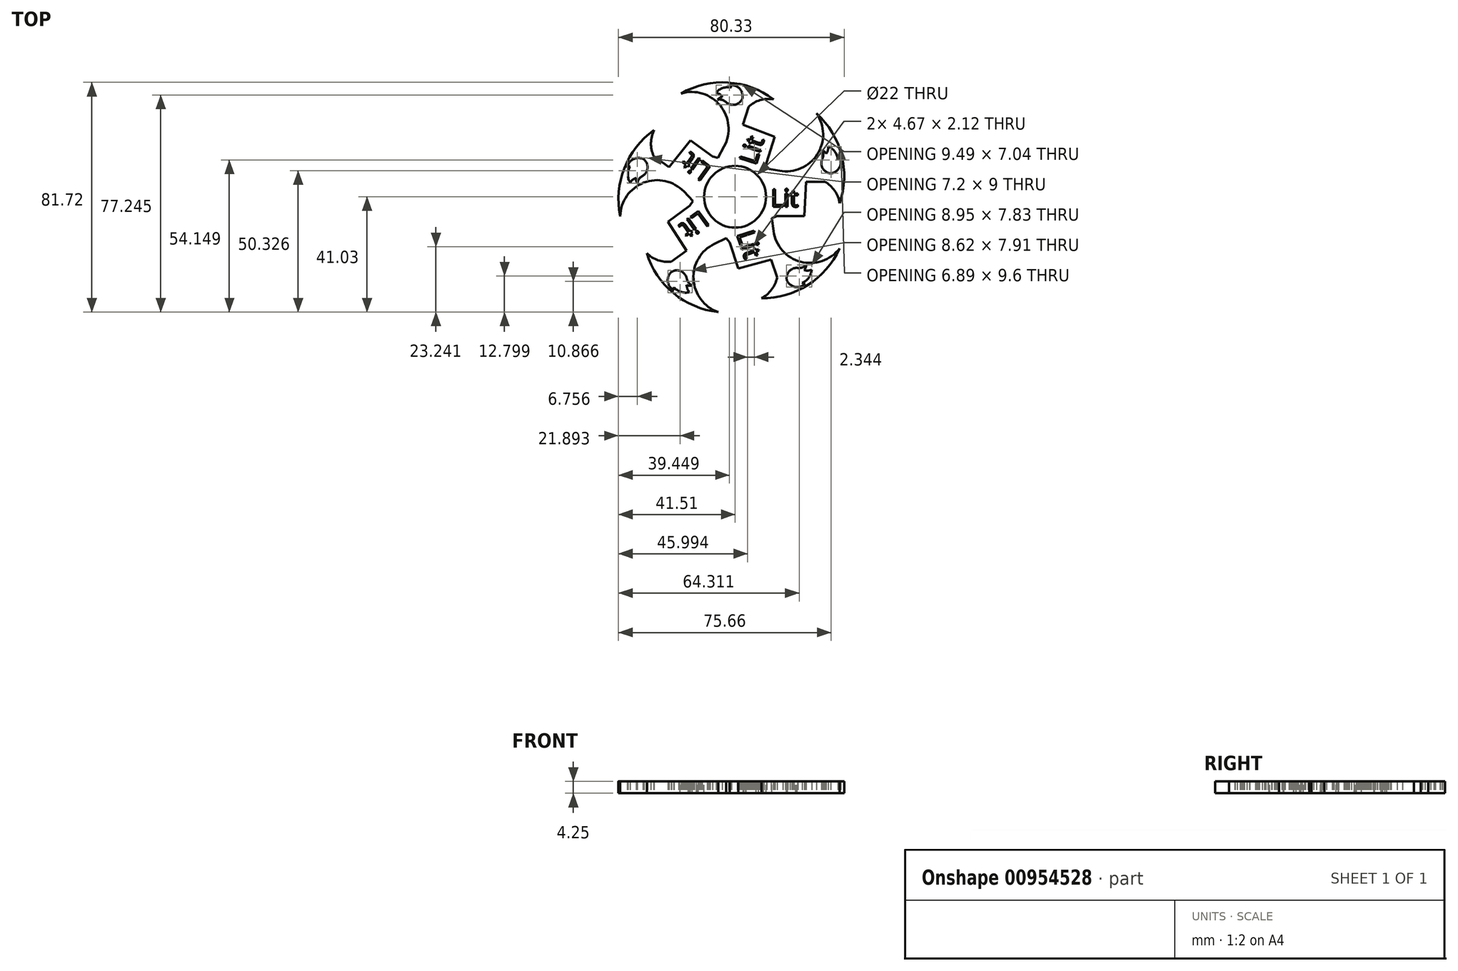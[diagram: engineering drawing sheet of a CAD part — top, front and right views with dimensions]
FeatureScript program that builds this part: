
annotation { "Feature Type Name" : "Feature", "Feature Type Description" : "" }
export const myFeature = defineFeature(function(context is Context, id is Id, definition is map)
    precondition{}
    {
        {
            var Q0;
            Q0=qCreatedBy(makeId("Top.planeOp"),FACE);
            var sketch = newSketch(context, id + "F0", { "sketchPlane" : qUnion([Q0])});
            skCircle(sketch, "E0", {"center": v(0, 0) * mm, "radius": 11 * mm});
            skArc(sketch, "E1", {"start": v(5, 13.33) * mm, "mid": v(-14.23, -0.3) * mm, "end": v(5.54, -13.11) * mm});
            skLineSegment(sketch, "E2", {"start": v(5, 13.33) * mm, "end": v(18.62, 10.86) * mm});
            skLineSegment(sketch, "E3", {"start": v(17.57, -8.04) * mm, "end": v(5.54, -13.11) * mm});
            skArc(sketch, "E4", {"start": v(18.62, 10.86) * mm, "mid": v(34.38, 17.7) * mm, "end": v(34.12, 34.88) * mm});
            skArc(sketch, "E5", {"start": v(43.79, -2.66) * mm, "mid": v(44.56, 17.56) * mm, "end": v(34.12, 34.88) * mm});
            skArc(sketch, "E6", {"start": v(43.79, -2.66) * mm, "mid": v(41.71, 2.53) * mm, "end": v(37.56, 6.26) * mm});
            skLineSegment(sketch, "E7", {"start": v(28.99, -8.04) * mm, "end": v(17.57, -8.04) * mm});
            skText(sketch, "E8", { "text": "Lit", "fontName": "OpenSans-Regular.ttf"});
            skLineSegment(sketch, "E9", {"start": v(28.99, -8.04) * mm, "end": v(29.68, 6.26) * mm});
            skLineSegment(sketch, "E10", {"start": v(29.68, 6.26) * mm, "end": v(37.56, 6.26) * mm});
            skPoint(sketch, "E11.orphan", {"position": v(0, -15.45) * mm});
            skPoint(sketch, "E12.orphan", {"position": v(0, 14.24) * mm});
            skPoint(sketch, "E13", {"position": v(14.9, -0.51) * mm});
            skLineSegment(sketch, "E14", {"start": v(0, 0) * mm, "end": v(28.23, 0) * mm, "construction": true});
            skArc(sketch, "E15", {"start": v(53.93, 19) * mm, "mid": v(54.3, 14.66) * mm, "end": v(58.04, 12.4) * mm});
            skArc(sketch, "E16", {"start": v(53.93, 19) * mm, "mid": v(54.47, 21.2) * mm, "end": v(53.93, 23.4) * mm});
            skArc(sketch, "E17", {"start": v(55.9, 21.72) * mm, "mid": v(55.05, 22.72) * mm, "end": v(53.93, 23.4) * mm});
            skArc(sketch, "E18", {"start": v(55.9, 21.72) * mm, "mid": v(56.67, 23.38) * mm, "end": v(56.82, 25.2) * mm});
            skArc(sketch, "E19", {"start": v(61.39, 19) * mm, "mid": v(59.97, 22.75) * mm, "end": v(56.82, 25.2) * mm});
            skArc(sketch, "E20", {"start": v(61.39, 19) * mm, "mid": v(61.87, 19.5) * mm, "end": v(62.21, 20.1) * mm});
            skArc(sketch, "E21", {"start": v(58.04, 12.4) * mm, "mid": v(62.14, 15.17) * mm, "end": v(62.21, 20.1) * mm});
            skLineSegment(sketch, "E22", {"start": v(33.75, 10.42) * mm, "end": v(57.45, 17.7) * mm, "construction": true});
            const initialGuessF0  = {"E8": [0.0149, -0.0042, 1, 0, 0.0074]};
            skSetInitialGuess(sketch, initialGuessF0);
            skSolve(sketch);
        }
        {
            var Q0;
            {var subQ0=sQuery(id+"F0.wireOp",EDGE,"JTTCuKp4-XvGG-GW8C-2jKd-2rtZk9alwzh2");var subQ1=sQuery(id+"F0.wireOp",EDGE,"M8TAi26V-Dveo-5j7V-sgvR-S3i7NmxKgKMn");var subQ2=makeQuery(id+"F0.imprint","INTERSECT",VERTEX,{"derivedFrom":[subQ1,subQ0]});Q0=makeQuery(id+"F0.imprint","IMPRINT",FACE,{"disambiguationData":[TD([[makeQuery(id+"F0.imprint","IMPRINT",EDGE,{"disambiguationData":[TD([[subQ2,1.0]])],"derivedFrom":subQ1}),-1.0]])]});}
            var Q1;
            {var subQ0=sQuery(id+"F0.wireOp",EDGE,"JTTCuKp4-XvGG-GW8C-2jKd-2rtZk9alwzh2");var subQ1=sQuery(id+"F0.wireOp",EDGE,"M8TAi26V-Dveo-5j7V-sgvR-S3i7NmxKgKMn");var subQ2=makeQuery(id+"F0.imprint","INTERSECT",VERTEX,{"derivedFrom":[subQ1,subQ0]});Q1=makeQuery(id+"F0.imprint","IMPRINT",FACE,{"disambiguationData":[TD([[makeQuery(id+"F0.imprint","IMPRINT",EDGE,{"disambiguationData":[TD([[subQ2,1.0]])],"derivedFrom":subQ1}),1.0]])]});}
            var Q2;
            {var subQ0=sQuery(id+"F0.wireOp",EDGE,"JTTCuKp4-XvGG-GW8C-2jKd-2rtZk9alwzh2");var subQ1=makeQuery(id+"F0.imprint","INTERSECT",VERTEX,{"derivedFrom":[subQ0,sQuery(id+"F0.wireOp",EDGE,"E2")]});Q2=makeQuery(id+"F0.imprint","IMPRINT",FACE,{"disambiguationData":[TD([[makeQuery(id+"F0.imprint","IMPRINT",EDGE,{"disambiguationData":[TD([[subQ1,-1.0]])],"derivedFrom":subQ0}),1.0]])]});}
            var Q3;
            Q3=makeQuery(id+"F0.imprint","IMPRINT",FACE,{"disambiguationData":[TD([[makeQuery(id+"F0.imprint","IMPRINT",EDGE,{"derivedFrom":sQuery(id+"F0.wireOp",EDGE,"E0")}),-1.0]])]});
            extrude(context, id + "F1", {"entities" : qUnion([Q0, Q1, Q2, Q3]), "depth" : 5 * mm, "offsetDistance" : 25 * mm});
        }
        {
            var Q0;
            Q0=makeQuery(id+"F0.imprint","IMPRINT",FACE,{"disambiguationData":[TD([[makeQuery(id+"F0.imprint","IMPRINT",EDGE,{"derivedFrom":sQuery(id+"F0.wireOp",EDGE,"E15")}),1.0]])]});
            extrude(context, id + "F2", {"entities" : qUnion([Q0]), "endBound" : BoundingType.SYMMETRIC, "depth" : 25 * mm, "offsetDistance" : 25 * mm});
        }
        {
            var Q0;
            Q0=makeQuery(id+"F2.opExtrude","SWEPT_BODY",BODY,{"disambiguationData":[OSD([sQuery(id+"F0.wireOp",EDGE,"E15"),sQuery(id+"F0.wireOp",EDGE,"E16"),sQuery(id+"F0.wireOp",EDGE,"E17"),sQuery(id+"F0.wireOp",EDGE,"E18"),sQuery(id+"F0.wireOp",EDGE,"E19"),sQuery(id+"F0.wireOp",EDGE,"E20"),sQuery(id+"F0.wireOp",EDGE,"E21")])]});
            var Q1;
            Q1=makeQuery(id+"F2.opExtrude","CAP_VERTEX",VERTEX,{"disambiguationData":[OSD([sQuery(id+"F0.wireOp",EDGE,"E18"),sQuery(id+"F0.wireOp",EDGE,"E19")])],"isStart":false});
            transform(context, id + "F3", {"entities" : qUnion([Q0]), "transformType" : TransformType.SCALE_UNIFORMLY, "scale" : .75, "scalePoint" : qUnion([Q1]), "makeCopy" : false});
        }
        {
            var Q0;
            Q0=makeQuery(id+"F1.opExtrude","SWEPT_BODY",BODY,{"disambiguationData":[OSD([sQuery(id+"F0.wireOp",EDGE,"E0"),sQuery(id+"F0.wireOp",EDGE,"E1"),sQuery(id+"F0.wireOp",EDGE,"E2"),sQuery(id+"F0.wireOp",EDGE,"E3"),sQuery(id+"F0.wireOp",EDGE,"E4"),sQuery(id+"F0.wireOp",EDGE,"E5"),sQuery(id+"F0.wireOp",EDGE,"E6"),sQuery(id+"F0.wireOp",EDGE,"E7"),sQuery(id+"F0.wireOp",EDGE,"E8.sketch_text.stroke-0"),sQuery(id+"F0.wireOp",EDGE,"E8.sketch_text.stroke-1"),sQuery(id+"F0.wireOp",EDGE,"E8.sketch_text.stroke-2"),sQuery(id+"F0.wireOp",EDGE,"E8.sketch_text.stroke-3"),sQuery(id+"F0.wireOp",EDGE,"E8.sketch_text.stroke-4"),sQuery(id+"F0.wireOp",EDGE,"E8.sketch_text.stroke-5"),sQuery(id+"F0.wireOp",EDGE,"E8.sketch_text.stroke-6"),sQuery(id+"F0.wireOp",EDGE,"E8.sketch_text.stroke-7"),sQuery(id+"F0.wireOp",EDGE,"E8.sketch_text.stroke-8"),sQuery(id+"F0.wireOp",EDGE,"E8.sketch_text.stroke-9"),sQuery(id+"F0.wireOp",EDGE,"E8.sketch_text.stroke-10"),sQuery(id+"F0.wireOp",EDGE,"E8.sketch_text.stroke-11"),sQuery(id+"F0.wireOp",EDGE,"E8.sketch_text.stroke-12"),sQuery(id+"F0.wireOp",EDGE,"E8.sketch_text.stroke-13"),sQuery(id+"F0.wireOp",EDGE,"E8.sketch_text.stroke-14"),sQuery(id+"F0.wireOp",EDGE,"E8.sketch_text.stroke-15"),sQuery(id+"F0.wireOp",EDGE,"E8.sketch_text.stroke-16"),sQuery(id+"F0.wireOp",EDGE,"E8.sketch_text.stroke-17"),sQuery(id+"F0.wireOp",EDGE,"E8.sketch_text.stroke-18"),sQuery(id+"F0.wireOp",EDGE,"E8.sketch_text.stroke-19"),sQuery(id+"F0.wireOp",EDGE,"E8.sketch_text.stroke-20"),sQuery(id+"F0.wireOp",EDGE,"E8.sketch_text.stroke-21"),sQuery(id+"F0.wireOp",EDGE,"E8.sketch_text.stroke-22"),sQuery(id+"F0.wireOp",EDGE,"E8.sketch_text.stroke-23"),sQuery(id+"F0.wireOp",EDGE,"E8.sketch_text.stroke-24"),sQuery(id+"F0.wireOp",EDGE,"E8.sketch_text.stroke-25"),sQuery(id+"F0.wireOp",EDGE,"E8.sketch_text.stroke-26"),sQuery(id+"F0.wireOp",EDGE,"E8.sketch_text.stroke-27"),sQuery(id+"F0.wireOp",EDGE,"E8.sketch_text.stroke-28"),sQuery(id+"F0.wireOp",EDGE,"E8.sketch_text.stroke-29"),sQuery(id+"F0.wireOp",EDGE,"E8.sketch_text.stroke-30"),sQuery(id+"F0.wireOp",EDGE,"E8.sketch_text.stroke-31"),sQuery(id+"F0.wireOp",EDGE,"E8.sketch_text.stroke-32"),sQuery(id+"F0.wireOp",EDGE,"E8.sketch_text.stroke-33"),sQuery(id+"F0.wireOp",EDGE,"E8.sketch_text.stroke-34"),sQuery(id+"F0.wireOp",EDGE,"E8.sketch_text.stroke-35"),sQuery(id+"F0.wireOp",EDGE,"E8.sketch_text.stroke-36"),sQuery(id+"F0.wireOp",EDGE,"E9"),sQuery(id+"F0.wireOp",EDGE,"E10")])]});
            var Q1;
            Q1=sQuery(id+"F0.wireOp",VERTEX,"E14.start");
            transform(context, id + "F4", {"entities" : qUnion([Q0]), "transformType" : TransformType.SCALE_UNIFORMLY, "scale" : .85, "scalePoint" : qUnion([Q1]), "makeCopy" : false});
        }
        {
            var Q0;
            Q0=makeQuery(id+"F2.opExtrude","SWEPT_BODY",BODY,{"disambiguationData":[OSD([sQuery(id+"F0.wireOp",EDGE,"E15"),sQuery(id+"F0.wireOp",EDGE,"E16"),sQuery(id+"F0.wireOp",EDGE,"E17"),sQuery(id+"F0.wireOp",EDGE,"E18"),sQuery(id+"F0.wireOp",EDGE,"E19"),sQuery(id+"F0.wireOp",EDGE,"E20"),sQuery(id+"F0.wireOp",EDGE,"E21")])]});
            var Q1;
            Q1=sQuery(id+"F0.wireOp",EDGE,"E22");
            transform(context, id + "F5", {"entities" : qUnion([Q0]), "transformType" : TransformType.TRANSLATION_ENTITY, "oppositeDirectionEntity" : true, "transformLine" : qUnion([Q1]), "makeCopy" : false});
        }
        {
            var Q0;
            Q0=makeQuery(id+"F2.opExtrude","SWEPT_BODY",BODY,{"disambiguationData":[OSD([sQuery(id+"F0.wireOp",EDGE,"E15"),sQuery(id+"F0.wireOp",EDGE,"E16"),sQuery(id+"F0.wireOp",EDGE,"E17"),sQuery(id+"F0.wireOp",EDGE,"E18"),sQuery(id+"F0.wireOp",EDGE,"E19"),sQuery(id+"F0.wireOp",EDGE,"E20"),sQuery(id+"F0.wireOp",EDGE,"E21")])]});
            var Q1;
            Q1=makeQuery(id+"F1.opExtrude","SWEPT_BODY",BODY,{"disambiguationData":[OSD([sQuery(id+"F0.wireOp",EDGE,"E0"),sQuery(id+"F0.wireOp",EDGE,"E1"),sQuery(id+"F0.wireOp",EDGE,"E2"),sQuery(id+"F0.wireOp",EDGE,"E3"),sQuery(id+"F0.wireOp",EDGE,"E4"),sQuery(id+"F0.wireOp",EDGE,"E5"),sQuery(id+"F0.wireOp",EDGE,"E6"),sQuery(id+"F0.wireOp",EDGE,"E7"),sQuery(id+"F0.wireOp",EDGE,"E8.sketch_text.stroke-0"),sQuery(id+"F0.wireOp",EDGE,"E8.sketch_text.stroke-1"),sQuery(id+"F0.wireOp",EDGE,"E8.sketch_text.stroke-2"),sQuery(id+"F0.wireOp",EDGE,"E8.sketch_text.stroke-3"),sQuery(id+"F0.wireOp",EDGE,"E8.sketch_text.stroke-4"),sQuery(id+"F0.wireOp",EDGE,"E8.sketch_text.stroke-5"),sQuery(id+"F0.wireOp",EDGE,"E8.sketch_text.stroke-6"),sQuery(id+"F0.wireOp",EDGE,"E8.sketch_text.stroke-7"),sQuery(id+"F0.wireOp",EDGE,"E8.sketch_text.stroke-8"),sQuery(id+"F0.wireOp",EDGE,"E8.sketch_text.stroke-9"),sQuery(id+"F0.wireOp",EDGE,"E8.sketch_text.stroke-10"),sQuery(id+"F0.wireOp",EDGE,"E8.sketch_text.stroke-11"),sQuery(id+"F0.wireOp",EDGE,"E8.sketch_text.stroke-12"),sQuery(id+"F0.wireOp",EDGE,"E8.sketch_text.stroke-13"),sQuery(id+"F0.wireOp",EDGE,"E8.sketch_text.stroke-14"),sQuery(id+"F0.wireOp",EDGE,"E8.sketch_text.stroke-15"),sQuery(id+"F0.wireOp",EDGE,"E8.sketch_text.stroke-16"),sQuery(id+"F0.wireOp",EDGE,"E8.sketch_text.stroke-17"),sQuery(id+"F0.wireOp",EDGE,"E8.sketch_text.stroke-18"),sQuery(id+"F0.wireOp",EDGE,"E8.sketch_text.stroke-19"),sQuery(id+"F0.wireOp",EDGE,"E8.sketch_text.stroke-20"),sQuery(id+"F0.wireOp",EDGE,"E8.sketch_text.stroke-21"),sQuery(id+"F0.wireOp",EDGE,"E8.sketch_text.stroke-22"),sQuery(id+"F0.wireOp",EDGE,"E8.sketch_text.stroke-23"),sQuery(id+"F0.wireOp",EDGE,"E8.sketch_text.stroke-24"),sQuery(id+"F0.wireOp",EDGE,"E8.sketch_text.stroke-25"),sQuery(id+"F0.wireOp",EDGE,"E8.sketch_text.stroke-26"),sQuery(id+"F0.wireOp",EDGE,"E8.sketch_text.stroke-27"),sQuery(id+"F0.wireOp",EDGE,"E8.sketch_text.stroke-28"),sQuery(id+"F0.wireOp",EDGE,"E8.sketch_text.stroke-29"),sQuery(id+"F0.wireOp",EDGE,"E8.sketch_text.stroke-30"),sQuery(id+"F0.wireOp",EDGE,"E8.sketch_text.stroke-31"),sQuery(id+"F0.wireOp",EDGE,"E8.sketch_text.stroke-32"),sQuery(id+"F0.wireOp",EDGE,"E8.sketch_text.stroke-33"),sQuery(id+"F0.wireOp",EDGE,"E8.sketch_text.stroke-34"),sQuery(id+"F0.wireOp",EDGE,"E8.sketch_text.stroke-35"),sQuery(id+"F0.wireOp",EDGE,"E8.sketch_text.stroke-36"),sQuery(id+"F0.wireOp",EDGE,"E9"),sQuery(id+"F0.wireOp",EDGE,"E10")])]});
            booleanBodies(context, id + "F6", {"operationType" : BooleanOperationType.SUBTRACTION, "tools" : qUnion([Q0]), "targets" : qUnion([Q1])});
        }
        {
            var Q0;
            Q0=makeQuery(id+"F1.opExtrude","SWEPT_BODY",BODY,{"disambiguationData":[OSD([sQuery(id+"F0.wireOp",EDGE,"E0"),sQuery(id+"F0.wireOp",EDGE,"E1"),sQuery(id+"F0.wireOp",EDGE,"E2"),sQuery(id+"F0.wireOp",EDGE,"E3"),sQuery(id+"F0.wireOp",EDGE,"E4"),sQuery(id+"F0.wireOp",EDGE,"E5"),sQuery(id+"F0.wireOp",EDGE,"E6"),sQuery(id+"F0.wireOp",EDGE,"E7"),sQuery(id+"F0.wireOp",EDGE,"E8.sketch_text.stroke-0"),sQuery(id+"F0.wireOp",EDGE,"E8.sketch_text.stroke-1"),sQuery(id+"F0.wireOp",EDGE,"E8.sketch_text.stroke-2"),sQuery(id+"F0.wireOp",EDGE,"E8.sketch_text.stroke-3"),sQuery(id+"F0.wireOp",EDGE,"E8.sketch_text.stroke-4"),sQuery(id+"F0.wireOp",EDGE,"E8.sketch_text.stroke-5"),sQuery(id+"F0.wireOp",EDGE,"E8.sketch_text.stroke-6"),sQuery(id+"F0.wireOp",EDGE,"E8.sketch_text.stroke-7"),sQuery(id+"F0.wireOp",EDGE,"E8.sketch_text.stroke-8"),sQuery(id+"F0.wireOp",EDGE,"E8.sketch_text.stroke-9"),sQuery(id+"F0.wireOp",EDGE,"E8.sketch_text.stroke-10"),sQuery(id+"F0.wireOp",EDGE,"E8.sketch_text.stroke-11"),sQuery(id+"F0.wireOp",EDGE,"E8.sketch_text.stroke-12"),sQuery(id+"F0.wireOp",EDGE,"E8.sketch_text.stroke-13"),sQuery(id+"F0.wireOp",EDGE,"E8.sketch_text.stroke-14"),sQuery(id+"F0.wireOp",EDGE,"E8.sketch_text.stroke-15"),sQuery(id+"F0.wireOp",EDGE,"E8.sketch_text.stroke-16"),sQuery(id+"F0.wireOp",EDGE,"E8.sketch_text.stroke-17"),sQuery(id+"F0.wireOp",EDGE,"E8.sketch_text.stroke-18"),sQuery(id+"F0.wireOp",EDGE,"E8.sketch_text.stroke-19"),sQuery(id+"F0.wireOp",EDGE,"E8.sketch_text.stroke-20"),sQuery(id+"F0.wireOp",EDGE,"E8.sketch_text.stroke-21"),sQuery(id+"F0.wireOp",EDGE,"E8.sketch_text.stroke-22"),sQuery(id+"F0.wireOp",EDGE,"E8.sketch_text.stroke-23"),sQuery(id+"F0.wireOp",EDGE,"E8.sketch_text.stroke-24"),sQuery(id+"F0.wireOp",EDGE,"E8.sketch_text.stroke-25"),sQuery(id+"F0.wireOp",EDGE,"E8.sketch_text.stroke-26"),sQuery(id+"F0.wireOp",EDGE,"E8.sketch_text.stroke-27"),sQuery(id+"F0.wireOp",EDGE,"E8.sketch_text.stroke-28"),sQuery(id+"F0.wireOp",EDGE,"E8.sketch_text.stroke-29"),sQuery(id+"F0.wireOp",EDGE,"E8.sketch_text.stroke-30"),sQuery(id+"F0.wireOp",EDGE,"E8.sketch_text.stroke-31"),sQuery(id+"F0.wireOp",EDGE,"E8.sketch_text.stroke-32"),sQuery(id+"F0.wireOp",EDGE,"E8.sketch_text.stroke-33"),sQuery(id+"F0.wireOp",EDGE,"E8.sketch_text.stroke-34"),sQuery(id+"F0.wireOp",EDGE,"E8.sketch_text.stroke-35"),sQuery(id+"F0.wireOp",EDGE,"E8.sketch_text.stroke-36"),sQuery(id+"F0.wireOp",EDGE,"E9"),sQuery(id+"F0.wireOp",EDGE,"E10")])]});
            var Q1;
            Q1=makeQuery(id+"F1.opExtrude","CAP_EDGE",EDGE,{"disambiguationData":[OSD([sQuery(id+"F0.wireOp",EDGE,"E0")])],"isStart":false});
            circularPattern(context, id + "F7", {"operationType" : NewBodyOperationType.ADD, "entities" : qUnion([Q0]), "axis" : qUnion([Q1]), "angle" : 360 * degree, "instanceCount" : 5, "equalSpace" : true});
        }
        {
            var Q0;
            {var subQ0=makeQuery(id+"F1.opExtrude","CAP_FACE",FACE,{"disambiguationData":[OSD([sQuery(id+"F0.wireOp",EDGE,"E0"),sQuery(id+"F0.wireOp",EDGE,"E1"),sQuery(id+"F0.wireOp",EDGE,"E2"),sQuery(id+"F0.wireOp",EDGE,"E3"),sQuery(id+"F0.wireOp",EDGE,"E4"),sQuery(id+"F0.wireOp",EDGE,"E5"),sQuery(id+"F0.wireOp",EDGE,"E6"),sQuery(id+"F0.wireOp",EDGE,"E7"),sQuery(id+"F0.wireOp",EDGE,"E8.sketch_text.stroke-0"),sQuery(id+"F0.wireOp",EDGE,"E8.sketch_text.stroke-1"),sQuery(id+"F0.wireOp",EDGE,"E8.sketch_text.stroke-2"),sQuery(id+"F0.wireOp",EDGE,"E8.sketch_text.stroke-3"),sQuery(id+"F0.wireOp",EDGE,"E8.sketch_text.stroke-4"),sQuery(id+"F0.wireOp",EDGE,"E8.sketch_text.stroke-5"),sQuery(id+"F0.wireOp",EDGE,"E8.sketch_text.stroke-6"),sQuery(id+"F0.wireOp",EDGE,"E8.sketch_text.stroke-7"),sQuery(id+"F0.wireOp",EDGE,"E8.sketch_text.stroke-8"),sQuery(id+"F0.wireOp",EDGE,"E8.sketch_text.stroke-9"),sQuery(id+"F0.wireOp",EDGE,"E8.sketch_text.stroke-10"),sQuery(id+"F0.wireOp",EDGE,"E8.sketch_text.stroke-11"),sQuery(id+"F0.wireOp",EDGE,"E8.sketch_text.stroke-12"),sQuery(id+"F0.wireOp",EDGE,"E8.sketch_text.stroke-13"),sQuery(id+"F0.wireOp",EDGE,"E8.sketch_text.stroke-14"),sQuery(id+"F0.wireOp",EDGE,"E8.sketch_text.stroke-15"),sQuery(id+"F0.wireOp",EDGE,"E8.sketch_text.stroke-16"),sQuery(id+"F0.wireOp",EDGE,"E8.sketch_text.stroke-17"),sQuery(id+"F0.wireOp",EDGE,"E8.sketch_text.stroke-18"),sQuery(id+"F0.wireOp",EDGE,"E8.sketch_text.stroke-19"),sQuery(id+"F0.wireOp",EDGE,"E8.sketch_text.stroke-20"),sQuery(id+"F0.wireOp",EDGE,"E8.sketch_text.stroke-21"),sQuery(id+"F0.wireOp",EDGE,"E8.sketch_text.stroke-22"),sQuery(id+"F0.wireOp",EDGE,"E8.sketch_text.stroke-23"),sQuery(id+"F0.wireOp",EDGE,"E8.sketch_text.stroke-24"),sQuery(id+"F0.wireOp",EDGE,"E8.sketch_text.stroke-25"),sQuery(id+"F0.wireOp",EDGE,"E8.sketch_text.stroke-26"),sQuery(id+"F0.wireOp",EDGE,"E8.sketch_text.stroke-27"),sQuery(id+"F0.wireOp",EDGE,"E8.sketch_text.stroke-28"),sQuery(id+"F0.wireOp",EDGE,"E8.sketch_text.stroke-29"),sQuery(id+"F0.wireOp",EDGE,"E8.sketch_text.stroke-30"),sQuery(id+"F0.wireOp",EDGE,"E8.sketch_text.stroke-31"),sQuery(id+"F0.wireOp",EDGE,"E8.sketch_text.stroke-32"),sQuery(id+"F0.wireOp",EDGE,"E8.sketch_text.stroke-33"),sQuery(id+"F0.wireOp",EDGE,"E8.sketch_text.stroke-34"),sQuery(id+"F0.wireOp",EDGE,"E8.sketch_text.stroke-35"),sQuery(id+"F0.wireOp",EDGE,"E8.sketch_text.stroke-36"),sQuery(id+"F0.wireOp",EDGE,"E9"),sQuery(id+"F0.wireOp",EDGE,"E10")])],"isStart":false});Q0=makeQuery(id+"F7.boolean.opBoolean","MERGE",FACE,{"derivedFrom":[subQ0,makeQuery(id+"F7.opPattern","COPY",FACE,{"derivedFrom":subQ0,"instanceName":"1"}),makeQuery(id+"F7.opPattern","COPY",FACE,{"derivedFrom":subQ0,"instanceName":"2"}),makeQuery(id+"F7.opPattern","COPY",FACE,{"derivedFrom":subQ0,"instanceName":"3"}),makeQuery(id+"F7.opPattern","COPY",FACE,{"derivedFrom":subQ0,"instanceName":"4"})]});}
            var sketch = newSketch(context, id + "F8", { "sketchPlane" : qUnion([Q0])});
            skCircle(sketch, "E23", {"center": v(0, 0) * mm, "radius": 11 * mm});
            skSolve(sketch);
        }
        {
            var Q0;
            Q0 = qSketchRegion(id + "F8", true);
            extrude(context, id + "F9", {"entities" : qUnion([Q0]), "operationType" : NewBodyOperationType.REMOVE, "endBound" : BoundingType.THROUGH_ALL, "oppositeDirection" : true, "depth" : 25 * mm, "offsetDistance" : 25 * mm});
        }
    });
